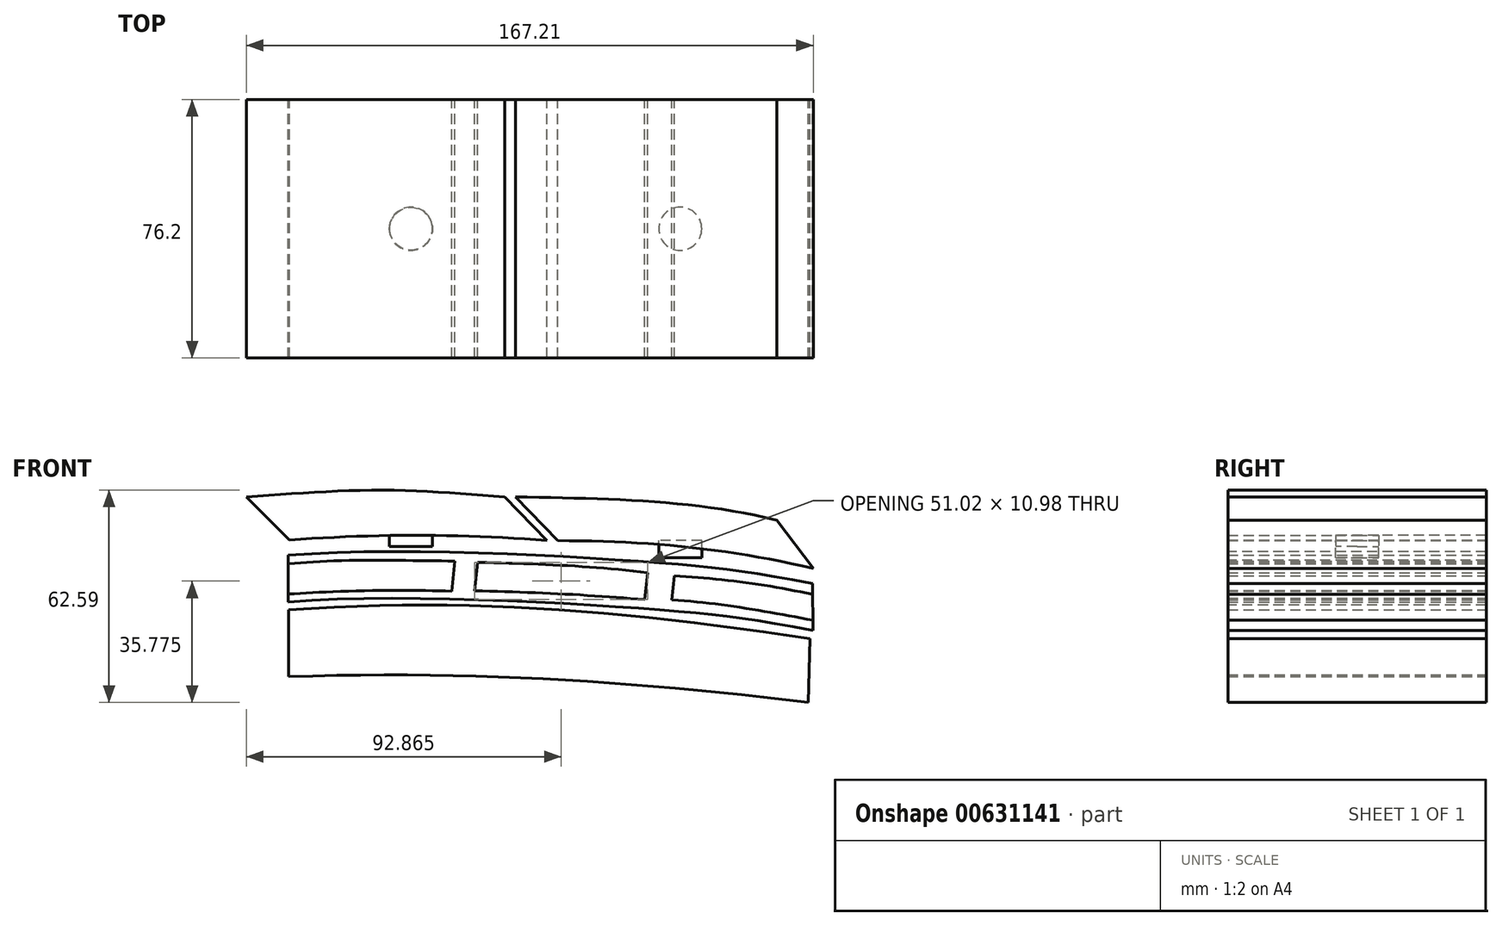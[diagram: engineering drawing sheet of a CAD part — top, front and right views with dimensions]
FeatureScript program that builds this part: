
annotation { "Feature Type Name" : "Feature", "Feature Type Description" : "" }
export const myFeature = defineFeature(function(context is Context, id is Id, definition is map)
    precondition{}
    {
        {
            var Q0;
            Q0=qCreatedBy(makeId("Front.planeOp"),FACE);
            var sketch = newSketch(context, id + "F0", { "sketchPlane" : qUnion([Q0])});
            skLineSegment(sketch, "E0", {"start": v(0, 0) * mm, "end": v(-12.5, 12.9) * mm});
            skLineSegment(sketch, "E1", {"start": v(-88.7, 12.9) * mm, "end": v(-76, 0.2) * mm});
            skFitSpline(sketch, "E2", {"points": [v(-88.7, 12.9) * mm, v(-49.6, 14.9) * mm, v(-12.5, 12.9) * mm], "startDerivative": vector(76.13, 5.42) * mm, "endDerivative": vector(75.38, -5.75) * mm});
            skFitSpline(sketch, "E3", {"points": [v(-76, 0.2) * mm, v(-37.79, 1.59) * mm, v(0.2, 0.04) * mm], "startDerivative": vector(76.13, 5.5) * mm, "endDerivative": vector(75.37, -5.82) * mm});
            skLineSegment(sketch, "E4", {"start": v(-9.34, 12.9) * mm, "end": v(3.16, 0) * mm});
            skFitSpline(sketch, "E5", {"points": [v(-9.34, 12.9) * mm, v(67.73, 6.03) * mm], "startDerivative": vector(80.06, -1.51) * mm, "endDerivative": vector(73.75, -18.55) * mm});
            skFitSpline(sketch, "E6", {"points": [v(3.16, 0) * mm, v(78.51, -8.22) * mm], "startDerivative": vector(77.5, 0) * mm, "endDerivative": vector(74.3, -17.92) * mm});
            skLineSegment(sketch, "E7", {"start": v(67.73, 6.03) * mm, "end": v(78.51, -8.22) * mm});
            skSolve(sketch);
        }
        {
            var Q0;
            {var subQ1=sQuery(id+"F0.wireOp",EDGE,"E1");Q0=makeQuery(id+"F0.imprint","IMPRINT",FACE,{"disambiguationData":[TD([[makeQuery(id+"F0.imprint","IMPRINT",EDGE,{"derivedFrom":subQ1}),1.0]])]});}
            var Q1;
            {var subQ3=sQuery(id+"F0.wireOp",EDGE,"E4");Q1=makeQuery(id+"F0.imprint","IMPRINT",FACE,{"disambiguationData":[TD([[makeQuery(id+"F0.imprint","IMPRINT",EDGE,{"derivedFrom":subQ3}),1.0]])]});}
            extrude(context, id + "F1", {"entities" : qUnion([Q0, Q1]), "depth" : 76.2 * mm, "offsetDistance" : 25.4 * mm});
        }
        {
            var Q0;
            Q0=qCreatedBy(makeId("Top.planeOp"),FACE);
            var sketch = newSketch(context, id + "F2", { "sketchPlane" : qUnion([Q0])});
            skCircle(sketch, "E8", {"center": v(-40.17, -38.1) * mm, "radius": 6.35 * mm});
            skCircle(sketch, "E9", {"center": v(39.27, -38.1) * mm, "radius": 6.35 * mm});
            skSolve(sketch);
        }
        {
            var Q0;
            Q0=makeQuery(id+"F2.imprint","IMPRINT",FACE,{"disambiguationData":[TD([[makeQuery(id+"F2.imprint","IMPRINT",EDGE,{"derivedFrom":sQuery(id+"F2.wireOp",EDGE,"E8")}),1.0]])]});
            extrude(context, id + "F3", {"entities" : qUnion([Q0]), "operationType" : NewBodyOperationType.ADD, "depth" : 1.78 * mm, "offsetDistance" : 25.4 * mm, "hasSecondDirection" : true, "secondDirectionOppositeDirection" : true, "secondDirectionDepth" : 1.78 * mm});
        }
        {
            var Q0;
            Q0=makeQuery(id+"F2.imprint","IMPRINT",FACE,{"disambiguationData":[TD([[makeQuery(id+"F2.imprint","IMPRINT",EDGE,{"derivedFrom":sQuery(id+"F2.wireOp",EDGE,"E9")}),1.0]])]});
            extrude(context, id + "F4", {"entities" : qUnion([Q0]), "depth" : 0 * mm, "offsetDistance" : 25.4 * mm, "hasSecondDirection" : true, "secondDirectionOppositeDirection" : true, "secondDirectionDepth" : 5.08 * mm});
        }
        {
            var Q0;
            Q0=qCreatedBy(makeId("Front.planeOp"),FACE);
            var sketch = newSketch(context, id + "F5", { "sketchPlane" : qUnion([Q0])});
            skFitSpline(sketch, "E10", {"points": [v(-76.33, -4.32) * mm, v(32.87, -6.5) * mm, v(78.32, -12.6) * mm], "startDerivative": vector(154.03, 13.17) * mm, "endDerivative": vector(146.48, -27.4) * mm});
            skFitSpline(sketch, "E11", {"points": [v(-76.33, -18.1) * mm, v(33, -20.36) * mm, v(78.44, -26.46) * mm], "startDerivative": vector(154.03, 13.17) * mm, "endDerivative": vector(146.48, -27.4) * mm});
            skLineSegment(sketch, "E12", {"start": v(78.32, -12.6) * mm, "end": v(78.35, -15.81) * mm});
            skLineSegment(sketch, "E13", {"start": v(-76.33, -18.1) * mm, "end": v(-76.33, -15.74) * mm});
            skLineSegment(sketch, "E14", {"start": v(-76.33, -4.32) * mm, "end": v(-76.33, -6.84) * mm});
            skFitSpline(sketch, "E15", {"points": [v(-76.33, -6.84) * mm, v(-62.93, -5.92) * mm, v(-43, -5.83) * mm, v(-27.24, -6.08) * mm, v(-13.28, -6.84) * mm], "startDerivative": vector(54.3, 4.86) * mm, "endDerivative": vector(58.92, -3.8) * mm});
            skFitSpline(sketch, "E16", {"points": [v(-76.33, -15.74) * mm, v(-63.18, -15.06) * mm, v(-43.17, -14.65) * mm, v(-28.14, -14.9) * mm, v(-14.67, -15.74) * mm], "startDerivative": vector(52.92, 3.15) * mm, "endDerivative": vector(64.3, -8.91) * mm});
            skLineSegment(sketch, "E17", {"start": v(-27.24, -6.08) * mm, "end": v(-28.14, -14.9) * mm});
            skLineSegment(sketch, "E18", {"start": v(-20.47, -6.41) * mm, "end": v(-21.34, -14.8) * mm});
            skFitSpline(sketch, "E19", {"points": [v(-20.47, -6.41) * mm, v(29.67, -9.44) * mm], "startDerivative": vector(50.98, -0.96) * mm, "endDerivative": vector(50.07, -6.03) * mm});
            skFitSpline(sketch, "E20", {"points": [v(-21.34, -14.8) * mm, v(28.74, -17.4) * mm], "startDerivative": vector(51, -1.04) * mm, "endDerivative": vector(46.74, -4.17) * mm});
            skLineSegment(sketch, "E21", {"start": v(29.67, -9.44) * mm, "end": v(28.74, -17.4) * mm});
            skFitSpline(sketch, "E22", {"points": [v(78.35, -15.81) * mm, v(37.51, -10.4) * mm], "startDerivative": vector(-40.83, 8.64) * mm, "endDerivative": vector(-39.68, 1.93) * mm});
            skFitSpline(sketch, "E23", {"points": [v(78.42, -23.47) * mm, v(36.83, -17.52) * mm], "startDerivative": vector(-40.74, 7.61) * mm, "endDerivative": vector(-42.16, 2.05) * mm});
            skLineSegment(sketch, "E24", {"start": v(37.51, -10.4) * mm, "end": v(36.83, -17.52) * mm});
            skLineSegment(sketch, "E25.trimOffspring", {"start": v(78.42, -23.47) * mm, "end": v(78.44, -26.46) * mm});
            skLineSegment(sketch, "E26", {"start": v(-76.33, -6.84) * mm, "end": v(-76.33, -15.74) * mm});
            skLineSegment(sketch, "E27", {"start": v(78.35, -15.81) * mm, "end": v(78.42, -23.47) * mm});
            skSolve(sketch);
        }
        {
            var Q0;
            Q0=makeQuery(id+"F5.imprint","IMPRINT",FACE,{"disambiguationData":[TD([[makeQuery(id+"F5.imprint","IMPRINT",EDGE,{"derivedFrom":sQuery(id+"F5.wireOp",EDGE,"E10")}),-1.0]])]});
            extrude(context, id + "F6", {"entities" : qUnion([Q0]), "depth" : 76.2 * mm, "offsetDistance" : 25.4 * mm});
        }
        {
            var Q0;
            Q0=makeQuery(id+"F5.imprint","IMPRINT",FACE,{"disambiguationData":[TD([[makeQuery(id+"F5.imprint","IMPRINT",EDGE,{"derivedFrom":sQuery(id+"F5.wireOp",EDGE,"E15")}),-1.0]])]});
            var Q1;
            Q1=makeQuery(id+"F5.imprint","IMPRINT",FACE,{"disambiguationData":[TD([[makeQuery(id+"F5.imprint","IMPRINT",EDGE,{"derivedFrom":sQuery(id+"F5.wireOp",EDGE,"E18")}),1.0]])]});
            var Q2;
            Q2=makeQuery(id+"F5.imprint","IMPRINT",FACE,{"disambiguationData":[TD([[makeQuery(id+"F5.imprint","IMPRINT",EDGE,{"derivedFrom":sQuery(id+"F5.wireOp",EDGE,"E22")}),1.0]])]});
            extrude(context, id + "F7", {"entities" : qUnion([Q0, Q1, Q2]), "depth" : 76.2 * mm, "offsetDistance" : 25.4 * mm});
        }
        {
            var Q0;
            Q0=qCreatedBy(makeId("Front.planeOp"),FACE);
            var sketch = newSketch(context, id + "F8", { "sketchPlane" : qUnion([Q0])});
            skLineSegment(sketch, "E28", {"start": v(-76.26, -20.4) * mm, "end": v(-76.26, -40.14) * mm});
            skFitSpline(sketch, "E29", {"points": [v(-76.26, -20.4) * mm, v(77.49, -28.87) * mm], "startDerivative": vector(156.17, 11.33) * mm, "endDerivative": vector(159.09, -24.28) * mm});
            skFitSpline(sketch, "E30", {"points": [v(-76.26, -40.14) * mm, v(77, -47.68) * mm], "startDerivative": vector(165.5, 5.9) * mm, "endDerivative": vector(151.65, -18.09) * mm});
            skLineSegment(sketch, "E31", {"start": v(77.49, -28.87) * mm, "end": v(77, -47.68) * mm});
            skSolve(sketch);
        }
        {
            var Q0;
            Q0=makeQuery(id+"F8.imprint","IMPRINT",FACE,{"disambiguationData":[TD([[makeQuery(id+"F8.imprint","IMPRINT",EDGE,{"derivedFrom":sQuery(id+"F8.wireOp",EDGE,"E28")}),1.0]])]});
            extrude(context, id + "F9", {"entities" : qUnion([Q0]), "depth" : 76.2 * mm, "offsetDistance" : 25.4 * mm});
        }
    });
